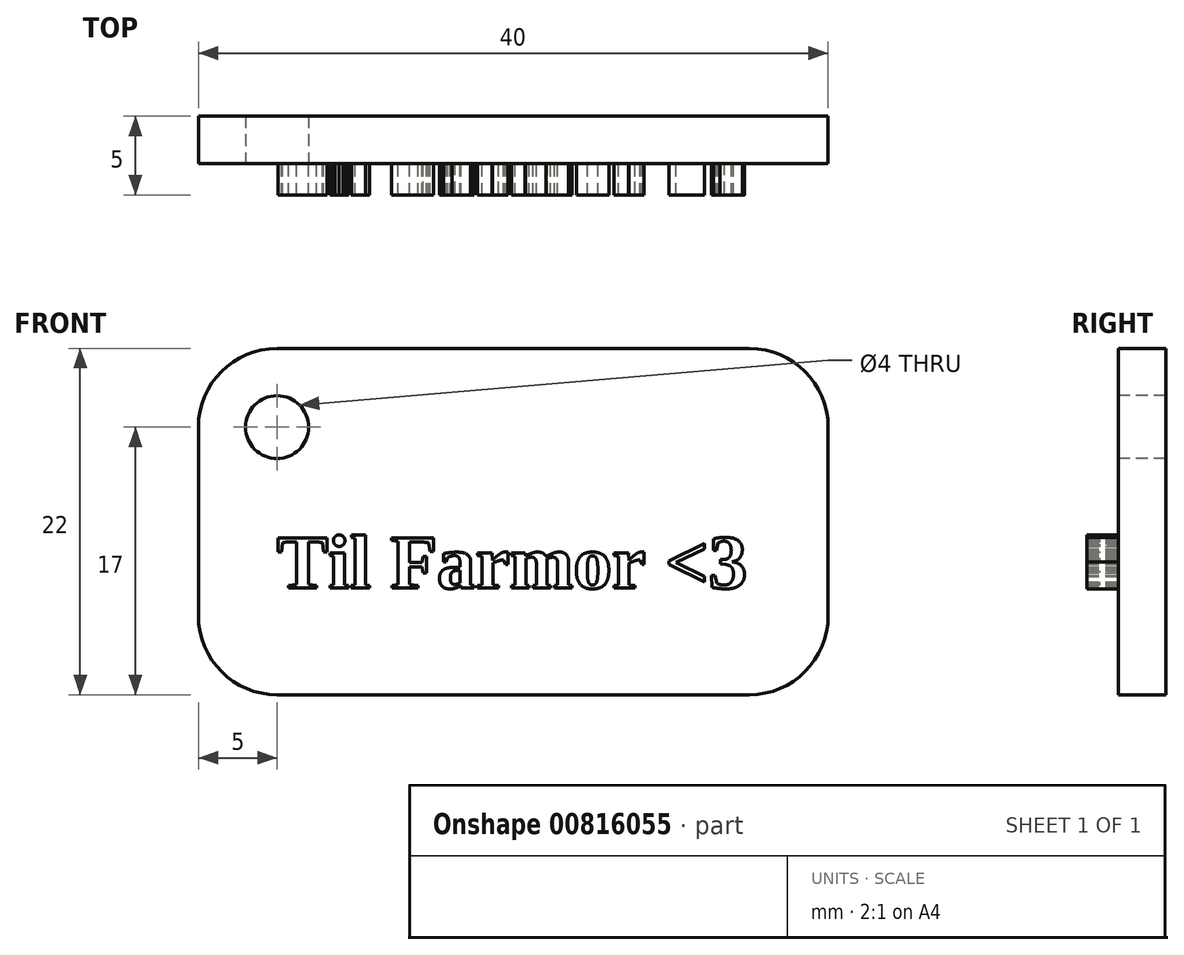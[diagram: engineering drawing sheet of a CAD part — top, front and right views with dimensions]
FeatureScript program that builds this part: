
annotation { "Feature Type Name" : "Feature", "Feature Type Description" : "" }
export const myFeature = defineFeature(function(context is Context, id is Id, definition is map)
    precondition{}
    {
        {
            var Q0;
            Q0=qCreatedBy(makeId("Front.planeOp"),FACE);
            var sketch = newSketch(context, id + "F0", { "sketchPlane" : qUnion([Q0])});
            skLineSegment(sketch, "E0.bottom", {"start": v(5, 0) * mm, "end": v(35, 0) * mm});
            skLineSegment(sketch, "E0.top", {"start": v(5, 22) * mm, "end": v(35, 22) * mm});
            skLineSegment(sketch, "E0.left", {"start": v(0, 5) * mm, "end": v(0, 17) * mm});
            skLineSegment(sketch, "E0.right", {"start": v(40, 5) * mm, "end": v(40, 17) * mm});
            skPoint(sketch, "E1.visualSharp", {"position": v(40, 22) * mm});
            skArc(sketch, "E1.filletArc", {"start": v(40, 17) * mm, "mid": v(38.54, 20.54) * mm, "end": v(35, 22) * mm});
            skPoint(sketch, "E2.visualSharp", {"position": v(40, 0) * mm});
            skArc(sketch, "E2.filletArc", {"start": v(35, 0) * mm, "mid": v(38.54, 1.46) * mm, "end": v(40, 5) * mm});
            skPoint(sketch, "E3.visualSharp", {"position": v(0, 0) * mm});
            skArc(sketch, "E3.filletArc", {"start": v(0, 5) * mm, "mid": v(1.46, 1.46) * mm, "end": v(5, 0) * mm});
            skPoint(sketch, "E4.visualSharp", {"position": v(0, 22) * mm});
            skArc(sketch, "E4.filletArc", {"start": v(5, 22) * mm, "mid": v(1.46, 20.54) * mm, "end": v(0, 17) * mm});
            skSolve(sketch);
        }
        {
            var Q0;
            Q0 = qSketchRegion(id + "F0", true);
            extrude(context, id + "F1", {"entities" : qUnion([Q0]), "depth" : 3 * mm, "offsetDistance" : 25 * mm});
        }
        {
            var Q0;
            Q0=makeQuery(id+"F1.opExtrude","CAP_FACE",FACE,{"disambiguationData":[OSD([sQuery(id+"F0.wireOp",EDGE,"E0.bottom"),sQuery(id+"F0.wireOp",EDGE,"E0.top"),sQuery(id+"F0.wireOp",EDGE,"E0.left"),sQuery(id+"F0.wireOp",EDGE,"E0.right"),sQuery(id+"F0.wireOp",EDGE,"E1.filletArc"),sQuery(id+"F0.wireOp",EDGE,"E2.filletArc"),sQuery(id+"F0.wireOp",EDGE,"E3.filletArc"),sQuery(id+"F0.wireOp",EDGE,"E4.filletArc")])],"isStart":false});
            var sketch = newSketch(context, id + "F2", { "sketchPlane" : qUnion([Q0])});
            skCircle(sketch, "E5", {"center": v(5, 17) * mm, "radius": 2 * mm});
            skSolve(sketch);
        }
        {
            var Q0;
            Q0 = qSketchRegion(id + "F2", true);
            extrude(context, id + "F3", {"entities" : qUnion([Q0]), "operationType" : NewBodyOperationType.REMOVE, "oppositeDirection" : true, "depth" : 25 * mm, "offsetDistance" : 25 * mm});
        }
        {
            var Q0;
            Q0=makeQuery(id+"F1.opExtrude","CAP_FACE",FACE,{"disambiguationData":[OSD([sQuery(id+"F0.wireOp",EDGE,"E0.bottom"),sQuery(id+"F0.wireOp",EDGE,"E0.top"),sQuery(id+"F0.wireOp",EDGE,"E0.left"),sQuery(id+"F0.wireOp",EDGE,"E0.right"),sQuery(id+"F0.wireOp",EDGE,"E1.filletArc"),sQuery(id+"F0.wireOp",EDGE,"E2.filletArc"),sQuery(id+"F0.wireOp",EDGE,"E3.filletArc"),sQuery(id+"F0.wireOp",EDGE,"E4.filletArc")])],"isStart":false});
            var sketch = newSketch(context, id + "F4", { "sketchPlane" : qUnion([Q0])});
            skText(sketch, "E6", { "text": "Til Farmor <3", "fontName": "Tinos-Bold.ttf"});
            skPoint(sketch, "E7", {"position": v(20, 0) * mm});
            const initialGuessF4  = {"E6": [0.005, 0.00677, 1, 0, 0.00351]};
            skSetInitialGuess(sketch, initialGuessF4);
            skSolve(sketch);
        }
        {
            var Q0;
            Q0 = qSketchRegion(id + "F4", true);
            extrude(context, id + "F5", {"entities" : qUnion([Q0]), "operationType" : NewBodyOperationType.ADD, "depth" : 2 * mm, "offsetDistance" : 25 * mm});
        }
    });
